# Revit family: Hager-Univers-IP65-D300-H550-Cl.II-encl-ES-es
name_source: partatom
category: Equipement électrique
units: mm (PartAtom-declared; Revit-internal decimal feet)

## family parameters
Configuration du panneau = Deux colonnes, circuits au sein
Cote de connecteur circulaire = Utiliser le diamètre
Couper avec des vides une fois chargée = Non
Hôte = Face
Partagée = Non
Point de calcul de pièce = Non
Type d'élément = Tableau de raccordement

## types (3) — shared parameters
Commentaires du type = Univers
EF000003 - Tipo de montaje = EV000384 - Montado superficial (escayola)
EF000007 - Color = EV000270 - Gris
EF000040 - Altura = 550 mm
EF000049 - Profundidad = 300 mm  [stored 0.984252 ft]
EF000116 - Número RAL = 7035
EF000118 - Con placa de montaje = Non
EF000266 - Número de filas = 3
EF001088 - Posibilidad de extensión = Non
EF001131 - Profundidad interna = 150 mm  [stored 0.492126 ft]
EF001596 - Material de la carcasa = EV000139 - Plástico
EF001613 - Integridad del circuito = EV000494 - Ninguno
EF003532 - Adecuado para uso en exteriores = Oui
EF004293 - Resistencia al impacto (IK) = EV008784 - IK10
EF004464 - Tipo de puerta = EV002646 - Único
EF005474 - Grado de protección (IP) = EV006421 - IP65
EF006244 - Tapa/puerta transparente = Non
EF006306 - Con cierre = Oui
EF007800 - Adecuado para la protección contra rayos = Oui
EF009170 - Espesor del material de la caja = 2 mm  [stored 0.00656168 ft]
EF009171 - Espesor puerta/tapa = 2 mm  [stored 0.00656168 ft]
EF009212 - Versión de la cubierta = EV000116 - Cerrado
EF015940 - Tapa con alivio de sobrepresión = Non
Fabricant = Hager
HG000002 - Con puerta o tapa = Oui
HG000003 - Gama = Univers
HG000006 - Empotrado = Non
HG000009 - Puerta batiente doble = Non
HG000010 - Puertas asimétricas = Non
HG000023 - Caja de doble sección = Non
HG000024 - Altura de la sección inferior = 800 mm
HG000026 - Instalación en suelo = Non
zero-valued in all types: EF000218 - Profundidad de instalación, EF000437 - Número de entradas de conductos de cables, EF009554 - Número de aberturas para placas-brida, Elévation par défaut, HG000027 - Altura de zócalo

## per-type parameters (varying)
| type | EF000008 - Anchura | EF000339 - Tipo de cubierta | EF002950 - Anchura de unidades de división | EF004427 - Número de módulos | EF008873 - Corriente nominal (In) | HG000004 - Referencia del fabricante |
| Montado superficial (escayola) IP65 A1100 A550 P300  - FL34S | 1100 mm | EV001012 - Cubrir | 48 | 144 | 630 A | FL34S |
| Montado superficial (escayola) IP65 A600 A550 P300  - FL32S | 600 mm | EV004216 - Puerta | 24 | 72 | 400 A | FL32S |
| Montado superficial (escayola) IP65 A850 A550 P300  - FL33S | 850 mm  [stored 2.78871 ft] | EV004216 - Puerta | 36 | 108 | 630 A | FL33S |

note: [stored X ft] marks values corroborated as IEEE doubles in the binary element streams (Revit-internal decimal feet)

## geometry (parser evidence)
native form markers: Sweep x10
no freeform markers — native parametric forms only
